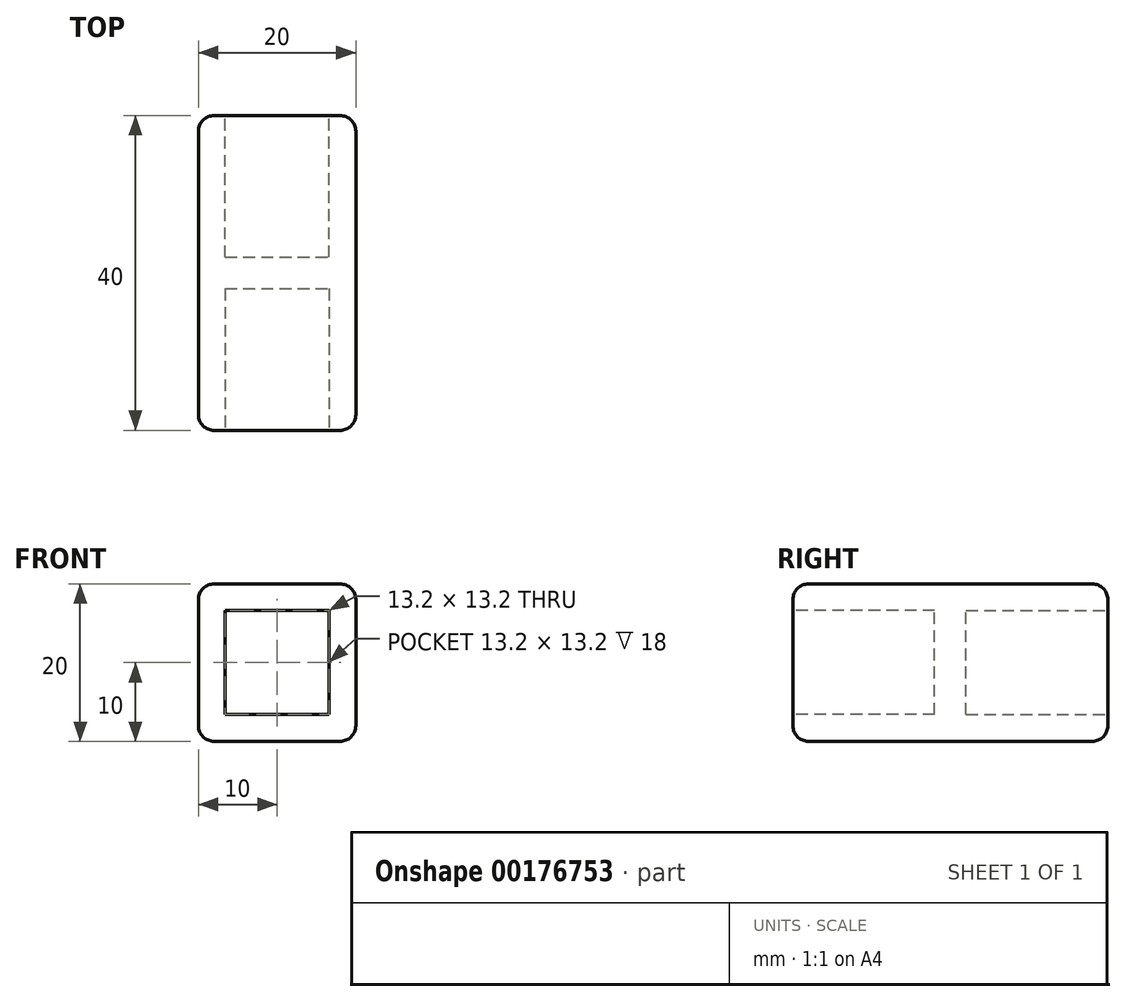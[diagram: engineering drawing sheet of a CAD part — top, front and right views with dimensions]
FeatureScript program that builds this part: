
annotation { "Feature Type Name" : "Feature", "Feature Type Description" : "" }
export const myFeature = defineFeature(function(context is Context, id is Id, definition is map)
    precondition{}
    {
        {
            var Q0;
            Q0=qCreatedBy(makeId("Front.planeOp"),FACE);
            var sketch = newSketch(context, id + "F0", { "sketchPlane" : qUnion([Q0])});
            skLineSegment(sketch, "E0.bottom", {"start": v(0, 0) * mm, "end": v(20, 0) * mm});
            skLineSegment(sketch, "E0.top", {"start": v(0, 20) * mm, "end": v(20, 20) * mm});
            skLineSegment(sketch, "E0.left", {"start": v(0, 0) * mm, "end": v(0, 20) * mm});
            skLineSegment(sketch, "E0.right", {"start": v(20, 0) * mm, "end": v(20, 20) * mm});
            skSolve(sketch);
        }
        {
            var Q0;
            Q0 = qSketchRegion(id + "F0", true);
            extrude(context, id + "F1", {"entities" : qUnion([Q0]), "depth" : 40 * mm});
        }
        {
            var Q0;
            Q0=makeQuery(id+"F1.opExtrude","CAP_FACE",FACE,{"disambiguationData":[OSD([sQuery(id+"F0.wireOp",EDGE,"E0.bottom"),sQuery(id+"F0.wireOp",EDGE,"E0.top"),sQuery(id+"F0.wireOp",EDGE,"E0.left"),sQuery(id+"F0.wireOp",EDGE,"E0.right")])],"isStart":true});
            var sketch = newSketch(context, id + "F2", { "sketchPlane" : qUnion([Q0])});
            skPoint(sketch, "E1", {"position": v(-3.4, 3.4) * mm});
            skLineSegment(sketch, "E2.bottom", {"start": v(-3.4, 3.4) * mm, "end": v(-16.6, 3.4) * mm});
            skLineSegment(sketch, "E2.top", {"start": v(-3.4, 16.6) * mm, "end": v(-16.6, 16.6) * mm});
            skLineSegment(sketch, "E2.left", {"start": v(-3.4, 3.4) * mm, "end": v(-3.4, 16.6) * mm});
            skLineSegment(sketch, "E2.right", {"start": v(-16.6, 3.4) * mm, "end": v(-16.6, 16.6) * mm});
            skSolve(sketch);
        }
        {
            var Q0;
            Q0=makeQuery(id+"F2.imprint","IMPRINT",FACE,{"disambiguationData":[TD([[makeQuery(id+"F2.imprint","IMPRINT",EDGE,{"derivedFrom":sQuery(id+"F2.wireOp",EDGE,"E2.bottom")}),-1.0]])]});
            extrude(context, id + "F3", {"entities" : qUnion([Q0]), "operationType" : NewBodyOperationType.REMOVE, "oppositeDirection" : true, "depth" : 18 * mm});
        }
        {
            var Q0;
            Q0=makeQuery(id+"F1.opExtrude","CAP_FACE",FACE,{"disambiguationData":[OSD([sQuery(id+"F0.wireOp",EDGE,"E0.bottom"),sQuery(id+"F0.wireOp",EDGE,"E0.top"),sQuery(id+"F0.wireOp",EDGE,"E0.left"),sQuery(id+"F0.wireOp",EDGE,"E0.right")])],"isStart":false});
            var sketch = newSketch(context, id + "F4", { "sketchPlane" : qUnion([Q0])});
            skPoint(sketch, "E3", {"position": v(3.4, 3.4) * mm});
            skLineSegment(sketch, "E4.bottom", {"start": v(3.4, 3.4) * mm, "end": v(16.6, 3.4) * mm});
            skLineSegment(sketch, "E4.top", {"start": v(3.4, 16.6) * mm, "end": v(16.6, 16.6) * mm});
            skLineSegment(sketch, "E4.left", {"start": v(3.4, 3.4) * mm, "end": v(3.4, 16.6) * mm});
            skLineSegment(sketch, "E4.right", {"start": v(16.6, 3.4) * mm, "end": v(16.6, 16.6) * mm});
            skSolve(sketch);
        }
        {
            var Q0;
            Q0=makeQuery(id+"F4.imprint","IMPRINT",FACE,{"disambiguationData":[TD([[makeQuery(id+"F4.imprint","IMPRINT",EDGE,{"derivedFrom":sQuery(id+"F4.wireOp",EDGE,"E4.bottom")}),1.0]])]});
            extrude(context, id + "F5", {"entities" : qUnion([Q0]), "operationType" : NewBodyOperationType.REMOVE, "oppositeDirection" : true, "depth" : 18 * mm});
        }
        {
            var Q0;
            Q0=makeQuery(id+"F1.opExtrude","SWEPT_FACE",FACE,{"disambiguationData":[OSD([sQuery(id+"F0.wireOp",EDGE,"E0.bottom")])]});
            var Q1;
            Q1=makeQuery(id+"F1.opExtrude","SWEPT_FACE",FACE,{"disambiguationData":[OSD([sQuery(id+"F0.wireOp",EDGE,"E0.left")])]});
            var Q2;
            Q2=makeQuery(id+"F1.opExtrude","SWEPT_FACE",FACE,{"disambiguationData":[OSD([sQuery(id+"F0.wireOp",EDGE,"E0.top")])]});
            var Q3;
            Q3=makeQuery(id+"F1.opExtrude","SWEPT_FACE",FACE,{"disambiguationData":[OSD([sQuery(id+"F0.wireOp",EDGE,"E0.right")])]});
            fillet(context, id + "F6", {"entities" : qUnion([Q0, Q1, Q2, Q3]), "radius" : 2 * mm, "tangentPropagation" : true, "allowEdgeOverflow" : false});
        }
    });
